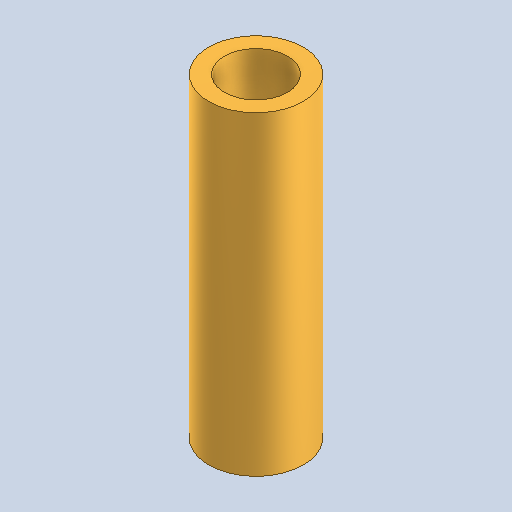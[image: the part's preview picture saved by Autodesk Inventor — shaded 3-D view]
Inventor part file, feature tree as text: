
AUTODESK INVENTOR PART (.ipt)
format: ipt  version: 2025 (Build 290162010, 162A)  size: 139,776 bytes
history: native  units: mm
features: extrude x1, sketch x1
ambient origin geometry x8: Origin, YZ Plane, XZ Plane, XY Plane, X Axis, Y Axis, Z Axis, Center Point
bodies: Volumenkörper1 (feature_tree)
feature tree (2):
  extrude  "Extrusion1"  Depth=20.0mm
  sketch  "Skizze1"  dims[d0=4.0mm d1=6.0mm d2=20.0mm d3=0.0mm]
